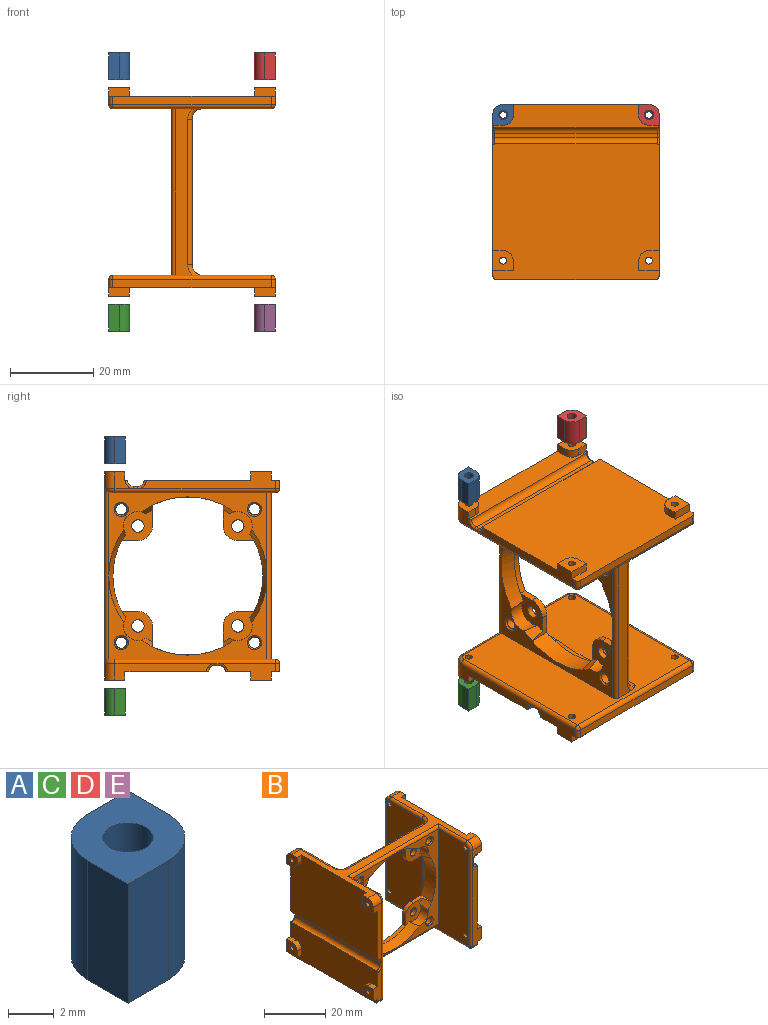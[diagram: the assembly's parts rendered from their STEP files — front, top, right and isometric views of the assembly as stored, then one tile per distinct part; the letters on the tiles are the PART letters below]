
ASSEMBLY  parts=5 mates=4
PART A: 9 faces, bbox 5x5x6.4 mm
  f0: plane 6.4x2.5mm, normal (1,0,0), area 16mm2, adj f1,f5,f6,f7
  f1: plane 6.4x2.5mm, normal (0,1,0), area 16mm2, adj f0,f2,f6,f7
  f2: cylinder r=2.5mm len=6.4mm, axis (0,0,-1), area 25.1mm2, adj f1,f3,f6,f7
  f3: plane 6.4x2.5mm, normal (-1,0,0), area 16mm2, adj f2,f4,f6,f7
  f4: plane 6.4x2.5mm, normal (0,-1,0), area 16mm2, adj f3,f5,f6,f7
  f5: cylinder r=2.5mm len=6.4mm, axis (0,0,-1), area 25.1mm2, adj f0,f4,f6,f7
  f6: plane 5x5mm, normal (0,0,1), area 18.5mm2, adj f0,f1,f2,f3,f4,f5,f8
  f7: plane 5x5mm, normal (0,0,-1), area 18.5mm2, adj f0,f1,f2,f3,f4,f5,f8
  f8: cylinder r=1.1mm len=6.4mm, axis (0,0,-1), area 44.2mm2, adj f6,f7
PART B: 166 faces, bbox 50.3x40.7x42.5 mm
  f0: plane 13.5x4mm, normal (0,-1,0), area 33.7mm2, adj f6,f11,f74,f77,f137,f141,f165
  f1: plane 13.5x4mm, normal (0,1,0), area 33.7mm2, adj f7,f11,f72,f73,f130,f131,f162
  f2: plane 33x4mm, normal (0,-1,0), area 72.7mm2, adj f9,f17,f89,f90,f132,f138,f159
  f3: plane 33x4mm, normal (0,1,0), area 72.7mm2, adj f8,f17,f91,f94,f126,f127,f156
  f4: plane 38x20mm, normal (0,-1,0), area 162.1mm2, adj f15,f21,f23,f25,f31,f44,f50,f52
  f5: plane 35x11.6mm, normal (0,1,0), area 187.5mm2, adj f27,f32,f33,f34,f35,f36,f37,f52
  f6: plane 4.9x2mm, normal (0,0,-1), area 9.8mm2, adj f0,f11,f76,f77
  f7: plane 4.9x2mm, normal (0,0,-1), area 9.8mm2, adj f1,f11,f70,f73
  f8: plane 4.9x2mm, normal (0,0,-1), area 9.8mm2, adj f3,f17,f93,f94
  f9: plane 4.9x2mm, normal (0,0,-1), area 9.8mm2, adj f2,f17,f87,f90
  f10: plane 40x5.5mm, normal (1,0,0), area 174.3mm2, adj f13,f16,f29,f83,f84,f85,f96,f97
  f11: plane 40x13mm, normal (-1,0,0), area 473.9mm2, adj f0,f1,f6,f7,f70,f71,f72,f74
  f12: plane 24x4mm, normal (0,1,0), area 49.7mm2, adj f18,f67,f69,f108,f130,f160
  f13: plane 4.5x4mm, normal (0,1,0), area 10.7mm2, adj f10,f95,f98,f99,f127,f154
  f14: plane 40.29x38.29mm, normal (-1,0,0), area 1222.4mm2, adj f22,f30,f100,f101,f102,f103,f114,f115
  f15: plane 40.29x38.29mm, normal (1,0,0), area 1222.4mm2, adj f4,f30,f104,f105,f106,f107,f117,f118
  f16: plane 50x35mm, normal (0,0,1), area 290.5mm2, adj f10,f18,f66,f69,f78,f81,f82,f85
  f17: plane 40x32.5mm, normal (1,0,0), area 1253.9mm2, adj f2,f3,f8,f9,f87,f88,f89,f91
  f18: plane 40x25mm, normal (-1,0,0), area 954.3mm2, adj f12,f16,f28,f66,f67,f68,f78,f79
  f19: cone r=19mm half-angle=15.9deg, axis (0,-1,0), area 8.9mm2, adj f22,f37,f46,f47
  f20: plane 35x11.6mm, normal (0,1,0), area 187.5mm2, adj f26,f38,f39,f40,f41,f42,f43,f52
  f21: cone r=19mm half-angle=15.9deg, axis (0,-1,0), area 8.9mm2, adj f4,f43,f50,f51
  f22: plane 38x20mm, normal (0,-1,0), area 162.1mm2, adj f14,f19,f23,f24,f25,f46,f48,f53
  f23: cone r=19mm half-angle=15.9deg, axis (0,-1,0), area 82.2mm2, adj f4,f22,f26,f48,f49,f50,f51
  f24: cone r=19mm half-angle=15.9deg, axis (0,-1,0), area 8.9mm2, adj f22,f38,f48,f49
  f25: cone r=19mm half-angle=15.9deg, axis (0,-1,0), area 82.2mm2, adj f4,f22,f27,f44,f45,f46,f47
  f26: cylinder r=18mm len=17mm, axis (0,-1,0), area 26.6mm2, adj f20,f23,f40,f41
  f27: cylinder r=18mm len=17mm, axis (0,-1,0), area 26.6mm2, adj f5,f25,f32,f35
  f28: plane 24x4mm, normal (0,-1,0), area 49.7mm2, adj f18,f80,f81,f109,f141,f163
  f29: plane 4.5x4mm, normal (0,-1,0), area 10.7mm2, adj f10,f82,f83,f86,f138,f157
  f30: plane 40x4.05mm, normal (0,0,-1), area 121.6mm2, adj f14,f15,f146,f147,f148,f149
  f31: cone r=19mm half-angle=15.9deg, axis (0,-1,0), area 8.9mm2, adj f4,f33,f44,f45
  f32: plane 3.87x1.5mm, normal (1,0,0), area 5.8mm2, adj f5,f27,f34,f45
  f33: plane 5.02x5.01mm, normal (0,0,-1), area 9.5mm2, adj f5,f31,f34,f45,f52
  f34: cylinder r=3.5mm len=3.5mm, axis (0,-1,0), area 8.2mm2, adj f5,f32,f33,f45
  f35: plane 3.87x1.5mm, normal (-1,0,0), area 5.8mm2, adj f5,f27,f36,f47
  f36: cylinder r=3.5mm len=3.5mm, axis (0,-1,0), area 8.2mm2, adj f5,f35,f37,f47
  f37: plane 5.02x5.01mm, normal (0,0,-1), area 9.5mm2, adj f5,f19,f36,f47,f53
  f38: plane 5.02x5.01mm, normal (0,0,1), area 9.5mm2, adj f20,f24,f39,f49,f53
  f39: cylinder r=3.5mm len=3.5mm, axis (0,-1,0), area 8.2mm2, adj f20,f38,f40,f49
  f40: plane 3.87x1.5mm, normal (-1,0,0), area 5.8mm2, adj f20,f26,f39,f49
  f41: plane 3.87x1.5mm, normal (1,0,0), area 5.8mm2, adj f20,f26,f42,f51
  f42: cylinder r=3.5mm len=3.5mm, axis (0,-1,0), area 8.2mm2, adj f20,f41,f43,f51
  f43: plane 5.02x5.01mm, normal (0,0,1), area 9.5mm2, adj f20,f21,f42,f51,f52
  f44: cylinder r=3.5mm len=5.43mm, axis (0,-1,0), area 29.4mm2, adj f4,f25,f31,f45
  f45: plane 7.37x7.37mm, normal (0,-1,0), area 35.7mm2, adj f25,f31,f32,f33,f34,f44,f65
  f46: cylinder r=3.5mm len=5.43mm, axis (0,-1,0), area 29.4mm2, adj f19,f22,f25,f47
  f47: plane 7.37x7.37mm, normal (0,-1,0), area 35.7mm2, adj f19,f25,f35,f36,f37,f46,f64
  f48: cylinder r=3.5mm len=5.43mm, axis (0,-1,0), area 29.4mm2, adj f22,f23,f24,f49
  f49: plane 7.37x7.37mm, normal (0,-1,0), area 35.7mm2, adj f23,f24,f38,f39,f40,f48,f63
  f50: cylinder r=3.5mm len=5.43mm, axis (0,-1,0), area 29.4mm2, adj f4,f21,f23,f51
  f51: plane 7.37x7.37mm, normal (0,-1,0), area 35.7mm2, adj f21,f23,f41,f42,f43,f50,f62
  f52: cylinder r=19mm len=17mm, axis (0,-1,0), area 88.1mm2, adj f4,f5,f20,f33,f43,f118
  f53: cylinder r=19mm len=17mm, axis (0,-1,0), area 88.1mm2, adj f5,f20,f22,f37,f38,f115
  f54: cylinder r=1.35mm len=4.58mm, axis (0,-1,0), area 38.9mm2, adj f5,f55
  f55: cone r=1.35mm half-angle=40deg, axis (0,-1,0), area 5.2mm2, adj f4,f54
  f56: cylinder r=1.35mm len=4.58mm, axis (0,-1,0), area 38.9mm2, adj f20,f57
  f57: cone r=1.35mm half-angle=40deg, axis (0,-1,0), area 5.2mm2, adj f22,f56
  f58: cylinder r=1.35mm len=4.58mm, axis (0,-1,0), area 38.9mm2, adj f5,f59
  f59: cone r=1.35mm half-angle=40deg, axis (0,-1,0), area 5.2mm2, adj f22,f58
  f60: cylinder r=1.35mm len=4.58mm, axis (0,-1,0), area 38.9mm2, adj f20,f61
  f61: cone r=1.35mm half-angle=40deg, axis (0,-1,0), area 5.2mm2, adj f4,f60
  f62: cylinder r=1.5mm len=3mm, axis (0,-1,0), area 14.1mm2, adj f20,f51
  f63: cylinder r=1.5mm len=3mm, axis (0,-1,0), area 14.1mm2, adj f20,f49
  f64: cylinder r=1.5mm len=3mm, axis (0,-1,0), area 14.1mm2, adj f5,f47
  f65: cylinder r=1.5mm len=3mm, axis (0,-1,0), area 14.1mm2, adj f5,f45
  f66: plane 2.5x2mm, normal (0,-1,0), area 5mm2, adj f16,f18,f68,f69
  f67: plane 2.5x2mm, normal (0,0,-1), area 5mm2, adj f12,f18,f68,f69
  f68: cylinder r=2.4mm len=2.4mm, axis (1,0,0), area 7.5mm2, adj f18,f66,f67,f69
  f69: plane 4.9x4.9mm, normal (-1,0,0), area 19.2mm2, adj f12,f16,f66,f67,f68,f107,f108
  f70: plane 2.5x2mm, normal (0,-1,0), area 5mm2, adj f7,f11,f71,f73
  f71: cylinder r=2.4mm len=2.4mm, axis (1,0,0), area 7.5mm2, adj f11,f70,f72,f73
  f72: plane 2.5x2mm, normal (0,0,1), area 5mm2, adj f1,f11,f71,f73
  f73: plane 4.9x4.9mm, normal (-1,0,0), area 20.5mm2, adj f1,f7,f70,f71,f72,f106
  f74: plane 2.5x2mm, normal (0,0,1), area 5mm2, adj f0,f11,f75,f77
  f75: cylinder r=2.4mm len=2.4mm, axis (1,0,0), area 7.5mm2, adj f11,f74,f76,f77
  f76: plane 2.5x2mm, normal (0,1,0), area 5mm2, adj f6,f11,f75,f77
  f77: plane 4.9x4.9mm, normal (-1,0,0), area 20.5mm2, adj f0,f6,f74,f75,f76,f105
  f78: plane 2.5x2mm, normal (0,1,0), area 5mm2, adj f16,f18,f79,f81
  f79: cylinder r=2.4mm len=2.4mm, axis (1,0,0), area 7.5mm2, adj f18,f78,f80,f81
  f80: plane 2.5x2mm, normal (0,0,-1), area 5mm2, adj f18,f28,f79,f81
  f81: plane 4.9x4.9mm, normal (-1,0,0), area 19.2mm2, adj f16,f28,f78,f79,f80,f104,f109
  f82: cylinder r=2.5mm len=4mm, axis (-1,0,0), area 15.7mm2, adj f16,f29,f86,f140
  f83: plane 2.5x2mm, normal (0,0,-1), area 5mm2, adj f10,f29,f84,f86
  f84: cylinder r=2.4mm len=2.4mm, axis (-1,0,0), area 7.5mm2, adj f10,f83,f85,f86
  f85: plane 2.5x2mm, normal (0,1,0), area 5mm2, adj f10,f16,f84,f86
  f86: plane 4.9x4.9mm, normal (1,0,0), area 19.2mm2, adj f16,f29,f82,f83,f84,f85,f103
  f87: plane 2.5x2mm, normal (0,1,0), area 5mm2, adj f9,f17,f88,f90
  f88: cylinder r=2.4mm len=2.4mm, axis (-1,0,0), area 7.5mm2, adj f17,f87,f89,f90
  f89: plane 2.5x2mm, normal (0,0,1), area 5mm2, adj f2,f17,f88,f90
  f90: plane 4.9x4.9mm, normal (1,0,0), area 20.5mm2, adj f2,f9,f87,f88,f89,f102
  f91: plane 2.5x2mm, normal (0,0,1), area 5mm2, adj f3,f17,f92,f94
  f92: cylinder r=2.4mm len=2.4mm, axis (-1,0,0), area 7.5mm2, adj f17,f91,f93,f94
  f93: plane 2.5x2mm, normal (0,-1,0), area 5mm2, adj f8,f17,f92,f94
  f94: plane 4.9x4.9mm, normal (1,0,0), area 20.5mm2, adj f3,f8,f91,f92,f93,f101
  f95: cylinder r=2.5mm len=4mm, axis (-1,0,0), area 15.7mm2, adj f13,f16,f99,f124
  f96: plane 2.5x2mm, normal (0,-1,0), area 5mm2, adj f10,f16,f97,f99
  f97: cylinder r=2.4mm len=2.4mm, axis (-1,0,0), area 7.5mm2, adj f10,f96,f98,f99
  f98: plane 2.5x2mm, normal (0,0,-1), area 5mm2, adj f10,f13,f97,f99
  f99: plane 4.9x4.9mm, normal (1,0,0), area 19.2mm2, adj f13,f16,f95,f96,f97,f98,f100
  f100: cylinder r=0.85mm len=5mm, axis (-1,0,0), area 26.7mm2, adj f14,f99
  f101: cylinder r=0.85mm len=5mm, axis (-1,0,0), area 26.7mm2, adj f14,f94
  f102: cylinder r=0.85mm len=5mm, axis (-1,0,0), area 26.7mm2, adj f14,f90
  f103: cylinder r=0.85mm len=5mm, axis (-1,0,0), area 26.7mm2, adj f14,f86
  f104: cylinder r=0.85mm len=5mm, axis (-1,0,0), area 26.7mm2, adj f15,f81
  f105: cylinder r=0.85mm len=5mm, axis (-1,0,0), area 26.7mm2, adj f15,f77
  f106: cylinder r=0.85mm len=5mm, axis (-1,0,0), area 26.7mm2, adj f15,f73
  f107: cylinder r=0.85mm len=5mm, axis (-1,0,0), area 26.7mm2, adj f15,f69
  f108: cylinder r=2.5mm len=4mm, axis (-1,0,0), area 15.7mm2, adj f12,f16,f69,f128
  f109: cylinder r=2.5mm len=4mm, axis (-1,0,0), area 15.7mm2, adj f16,f28,f81,f143
  f110: plane 39x1mm, normal (1,0,0), area 39mm2, adj f152,f153,f155,f158
  f111: plane 39x1mm, normal (-1,0,0), area 39mm2, adj f150,f151,f161,f164
  f112: plane 38x2mm, normal (0,0,-1), area 76mm2, adj f17,f126,f132,f133
  f113: plane 38x2mm, normal (0,0,-1), area 76mm2, adj f11,f131,f136,f137
  f114: cylinder r=2.5mm len=11.6mm, axis (0,0,1), area 45.6mm2, adj f14,f20,f115,f148
  f115: bspline ~14.8x2.5mm, area 42.6mm2, adj f14,f53,f114,f116
  f116: cylinder r=2.5mm len=11.6mm, axis (0,0,1), area 45.6mm2, adj f5,f14,f115,f120
  f117: cylinder r=2.5mm len=11.6mm, axis (0,0,1), area 45.6mm2, adj f15,f20,f118,f146
  f118: bspline ~16.32x2.95mm, area 42.6mm2, adj f15,f52,f117,f119
  f119: cylinder r=2.5mm len=11.6mm, axis (0,0,1), area 45.6mm2, adj f5,f15,f118,f123
  f120: torus R=3.5mm, axis (0,0,1), area 7.1mm2, adj f16,f116,f121,f122
  f121: cylinder r=1mm len=35mm, axis (1,0,0), area 55mm2, adj f5,f16,f120,f123
  f122: cylinder r=1mm len=15mm, axis (0,1,0), area 23.6mm2, adj f14,f16,f120,f124
  f123: torus R=3.5mm, axis (0,0,1), area 7.1mm2, adj f16,f119,f121,f125
  f124: torus R=1.5mm, axis (1,0,0), area 5.3mm2, adj f14,f95,f122,f127
  f125: cylinder r=1mm len=15mm, axis (0,-1,0), area 23.6mm2, adj f15,f16,f123,f128
  f126: cylinder r=1mm len=2mm, axis (1,0,0), area 3.1mm2, adj f3,f17,f112,f129
  f127: cylinder r=1mm len=38.5mm, axis (0,0,-1), area 60.5mm2, adj f3,f13,f14,f124,f129,f155
  f128: torus R=1.5mm, axis (-1,0,0), area 5.3mm2, adj f15,f108,f125,f130
  f129: sphere r=1mm, area 1.6mm2, adj f126,f127,f133
  f130: cylinder r=1mm len=38.5mm, axis (0,0,-1), area 60.5mm2, adj f1,f12,f15,f128,f134,f161
  f131: cylinder r=1mm len=2mm, axis (1,0,0), area 3.1mm2, adj f1,f11,f113,f134
  f132: cylinder r=1mm len=2mm, axis (-1,0,0), area 3.1mm2, adj f2,f17,f112,f135
  f133: cylinder r=1mm len=38mm, axis (0,1,0), area 59.7mm2, adj f14,f112,f129,f135
  f134: sphere r=1mm, area 1.6mm2, adj f130,f131,f136
  f135: sphere r=1mm, area 1.6mm2, adj f132,f133,f138
  f136: cylinder r=1mm len=38mm, axis (0,-1,0), area 59.7mm2, adj f15,f113,f134,f139
  f137: cylinder r=1mm len=2mm, axis (-1,0,0), area 3.1mm2, adj f0,f11,f113,f139
  f138: cylinder r=1mm len=38.5mm, axis (0,0,-1), area 60.5mm2, adj f2,f14,f29,f135,f140,f158
  f139: sphere r=1mm, area 1.6mm2, adj f136,f137,f141
  f140: torus R=1.5mm, axis (1,0,0), area 5.3mm2, adj f14,f82,f138,f142
  f141: cylinder r=1mm len=38.5mm, axis (0,0,-1), area 60.5mm2, adj f0,f15,f28,f139,f143,f164
  f142: cylinder r=1mm len=13.5mm, axis (0,1,0), area 20.4mm2, adj f14,f16,f140,f144
  f143: torus R=1.5mm, axis (-1,0,0), area 5.3mm2, adj f15,f109,f141,f145
  f144: cylinder r=1mm len=42mm, axis (-1,0,0), area 64.4mm2, adj f4,f16,f22,f142,f145
  f145: cylinder r=1mm len=13.5mm, axis (0,-1,0), area 20.4mm2, adj f15,f16,f143,f144
  f146: torus R=3.5mm, axis (0,0,1), area 5.2mm2, adj f15,f30,f117,f147
  f147: cylinder r=1mm len=35mm, axis (-1,0,0), area 55mm2, adj f20,f30,f146,f148
  f148: torus R=3.5mm, axis (0,0,1), area 5.2mm2, adj f14,f30,f114,f147
  f149: cylinder r=1mm len=40mm, axis (1,0,0), area 62.8mm2, adj f4,f14,f15,f22,f30
  f150: cylinder r=1.5mm len=39mm, axis (0,1,0), area 91.9mm2, adj f11,f111,f162,f165
  f151: cylinder r=1.5mm len=39mm, axis (0,1,0), area 91.9mm2, adj f18,f111,f160,f163
  f152: cylinder r=1.5mm len=39mm, axis (0,1,0), area 91.9mm2, adj f10,f110,f154,f157
  f153: cylinder r=1.5mm len=39mm, axis (0,1,0), area 91.9mm2, adj f17,f110,f156,f159
  f154: torus R=2mm, axis (0,-1,0), area 2.1mm2, adj f10,f13,f152,f155
  f155: cylinder r=0.5mm len=1mm, axis (0,0,-1), area 0.8mm2, adj f110,f127,f154,f156
  f156: torus R=2mm, axis (0,-1,0), area 2.1mm2, adj f3,f17,f153,f155
  f157: torus R=2mm, axis (0,1,0), area 2.1mm2, adj f10,f29,f152,f158
  f158: cylinder r=0.5mm len=1mm, axis (0,0,-1), area 0.8mm2, adj f110,f138,f157,f159
  f159: torus R=2mm, axis (0,1,0), area 2.1mm2, adj f2,f17,f153,f158
  f160: torus R=2mm, axis (0,-1,0), area 2.1mm2, adj f12,f18,f151,f161
  f161: cylinder r=0.5mm len=1mm, axis (0,0,1), area 0.8mm2, adj f111,f130,f160,f162
  f162: torus R=2mm, axis (0,-1,0), area 2.1mm2, adj f1,f11,f150,f161
  f163: torus R=2mm, axis (0,1,0), area 2.1mm2, adj f18,f28,f151,f164
  f164: cylinder r=0.5mm len=1mm, axis (0,0,1), area 0.8mm2, adj f111,f141,f163,f165
  f165: torus R=2mm, axis (0,1,0), area 2.1mm2, adj f0,f11,f150,f164
PART C: same geometry as A
PART D: same geometry as A
PART E: same geometry as A
PLACE A rot(axis=(0,0,1),180deg) t=(22.31,74.51,78.31)mm
PLACE B rot(axis=(-0.58,-0.58,-0.58),120deg) t=(-10.81,-24.81,79.79)mm
PLACE C t=(-20.17,-49.12,17.91)mm
PLACE D rot(axis=(1,0,0),180deg) t=(14.83,74.51,84.71)mm
PLACE E rot(axis=(1,0,0),180deg) t=(14.83,74.51,24.31)mm
MATE fastened B.f140 <-> C.f2  axis (0,0,-1) through (1.07,12.69,24.31)mm
MATE fastened B.f124 <-> E.f2  axis (0,0,-1) through (36.07,12.69,24.31)mm
MATE fastened A.f2 <-> B.f79  axis (0,0,-1) through (1.07,12.69,78.31)mm
MATE fastened B.f68 <-> D.f2  axis (0,0,1) through (36.07,12.69,78.31)mm
